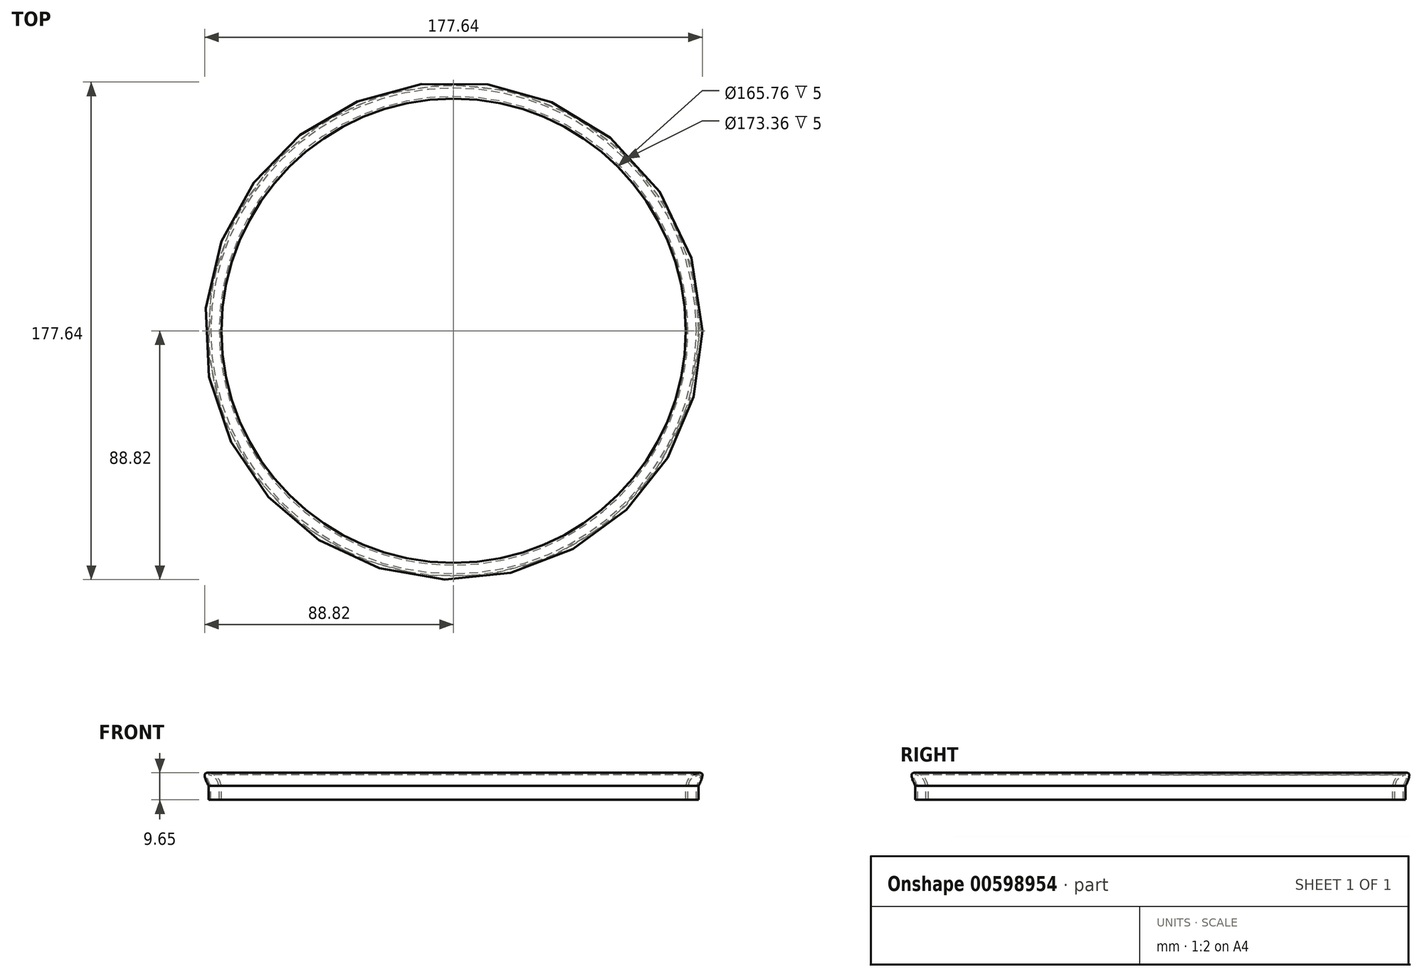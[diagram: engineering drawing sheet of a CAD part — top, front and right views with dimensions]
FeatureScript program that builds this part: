
annotation { "Feature Type Name" : "Feature", "Feature Type Description" : "" }
export const myFeature = defineFeature(function(context is Context, id is Id, definition is map)
    precondition{}
    {
        {
            var Q0;
            Q0=qCreatedBy(makeId("Front.planeOp"),FACE);
            var sketch = newSketch(context, id + "F0", { "sketchPlane" : qUnion([Q0])});
            skLineSegment(sketch, "E0", {"start": v(-87.48, 0) * mm, "end": v(-87.48, 5) * mm});
            skLineSegment(sketch, "E1", {"start": v(-86.68, 0) * mm, "end": v(-86.68, 5) * mm});
            skLineSegment(sketch, "E2", {"start": v(-83.68, 0) * mm, "end": v(-83.68, 5) * mm});
            skLineSegment(sketch, "E3", {"start": v(-82.88, 0) * mm, "end": v(-82.88, 5) * mm});
            skLineSegment(sketch, "E4", {"start": v(-83.68, 0) * mm, "end": v(-82.88, 0) * mm});
            skLineSegment(sketch, "E5", {"start": v(-86.68, 0) * mm, "end": v(-87.48, 0) * mm});
            skFitSpline(sketch, "E6", {"points": [v(-82.88, 5) * mm, v(-84.31, 7.98) * mm, v(-88.43, 9.55) * mm, v(-87.48, 5) * mm], "startDerivative": vector(-4.03, 10.63) * mm, "endDerivative": vector(9.74, -19.25) * mm});
            skFitSpline(sketch, "E7", {"points": [v(-83.68, 5) * mm, v(-84.61, 7.2) * mm, v(-87.8, 8.95) * mm, v(-86.68, 5) * mm], "startDerivative": vector(-4.56, 8.63) * mm, "endDerivative": vector(8.48, -16.96) * mm});
            skLineSegment(sketch, "E8", {"start": v(-88.95, -3.6) * mm, "end": v(-79.5, -3.6) * mm, "construction": true});
            skLineSegment(sketch, "E9.MirrorCS", {"start": v(-83.68, -7.2) * mm, "end": v(-83.68, -12.2) * mm});
            skLineSegment(sketch, "E10.MirrorCS", {"start": v(-82.88, -7.2) * mm, "end": v(-82.88, -12.2) * mm});
            skLineSegment(sketch, "E11.MirrorCS", {"start": v(-86.68, -7.2) * mm, "end": v(-86.68, -12.2) * mm});
            skLineSegment(sketch, "E12.MirrorCS", {"start": v(-87.48, -7.2) * mm, "end": v(-87.48, -12.2) * mm});
            skLineSegment(sketch, "E13.MirrorCS", {"start": v(-86.68, -7.2) * mm, "end": v(-87.48, -7.2) * mm});
            skLineSegment(sketch, "E14.MirrorCS", {"start": v(-83.68, -7.2) * mm, "end": v(-82.88, -7.2) * mm});
            skFitSpline(sketch, "E15.MirrorCS", {"points": [v(-82.88, -12.2) * mm, v(-84.31, -15.18) * mm, v(-88.43, -16.75) * mm, v(-87.48, -12.2) * mm], "startDerivative": vector(-4.03, -10.63) * mm, "endDerivative": vector(9.74, 19.25) * mm});
            skFitSpline(sketch, "E16.MirrorCS", {"points": [v(-83.68, -12.2) * mm, v(-84.61, -14.4) * mm, v(-87.8, -16.15) * mm, v(-86.68, -12.2) * mm], "startDerivative": vector(-4.56, -8.63) * mm, "endDerivative": vector(8.48, 16.96) * mm});
            skLineSegment(sketch, "E17", {"start": v(-86.68, -8.26) * mm, "end": v(-86.68, -4.2) * mm});
            skLineSegment(sketch, "E18", {"start": v(-86.68, -4.2) * mm, "end": v(-85.88, -4.2) * mm});
            skLineSegment(sketch, "E19", {"start": v(-85.88, -4.2) * mm, "end": v(-85.88, -8.26) * mm});
            skLineSegment(sketch, "E20", {"start": v(-85.88, -8.26) * mm, "end": v(-86.68, -8.26) * mm});
            skLineSegment(sketch, "E21", {"start": v(-83.68, -8.26) * mm, "end": v(-84.48, -8.26) * mm});
            skLineSegment(sketch, "E22", {"start": v(-84.48, -8.26) * mm, "end": v(-84.48, -4.2) * mm});
            skLineSegment(sketch, "E23", {"start": v(-84.48, -4.2) * mm, "end": v(-83.68, -4.2) * mm});
            skLineSegment(sketch, "E24", {"start": v(-83.68, -4.2) * mm, "end": v(-83.68, -7.2) * mm});
            skSolve(sketch);
        }
        {
            var Q0;
            Q0=qCreatedBy(makeId("Top.planeOp"),FACE);
            var sketch = newSketch(context, id + "F1", { "sketchPlane" : qUnion([Q0])});
            skCircle(sketch, "E25", {"center": v(0, 0) * mm, "radius": 13.52 * mm, "construction": true});
            skSolve(sketch);
        }
        {
            var Q0;
            Q0=sQuery(id+"F0.wireOp",EDGE,"E7");
            var Q1;
            Q1=sQuery(id+"F0.wireOp",EDGE,"E6");
            var Q2;
            Q2=sQuery(id+"F0.wireOp",EDGE,"E3");
            var Q3;
            Q3=sQuery(id+"F0.wireOp",EDGE,"E2");
            var Q4;
            Q4=sQuery(id+"F0.wireOp",EDGE,"E4");
            var Q5;
            Q5=sQuery(id+"F0.wireOp",EDGE,"E1");
            var Q6;
            Q6=sQuery(id+"F0.wireOp",EDGE,"E0");
            var Q7;
            Q7=sQuery(id+"F0.wireOp",EDGE,"E5");
            var Q8;
            Q8=sQuery(id+"F1.wireOp",EDGE,"E25");
            revolve(context, id + "F2", {"bodyType" : ToolBodyType.SURFACE, "surfaceEntities" : qUnion([Q0, Q1, Q2, Q3, Q4, Q5, Q6, Q7]), "axis" : qUnion([Q8]), "revolveType" : RevolveType.FULL});
        }
    });
